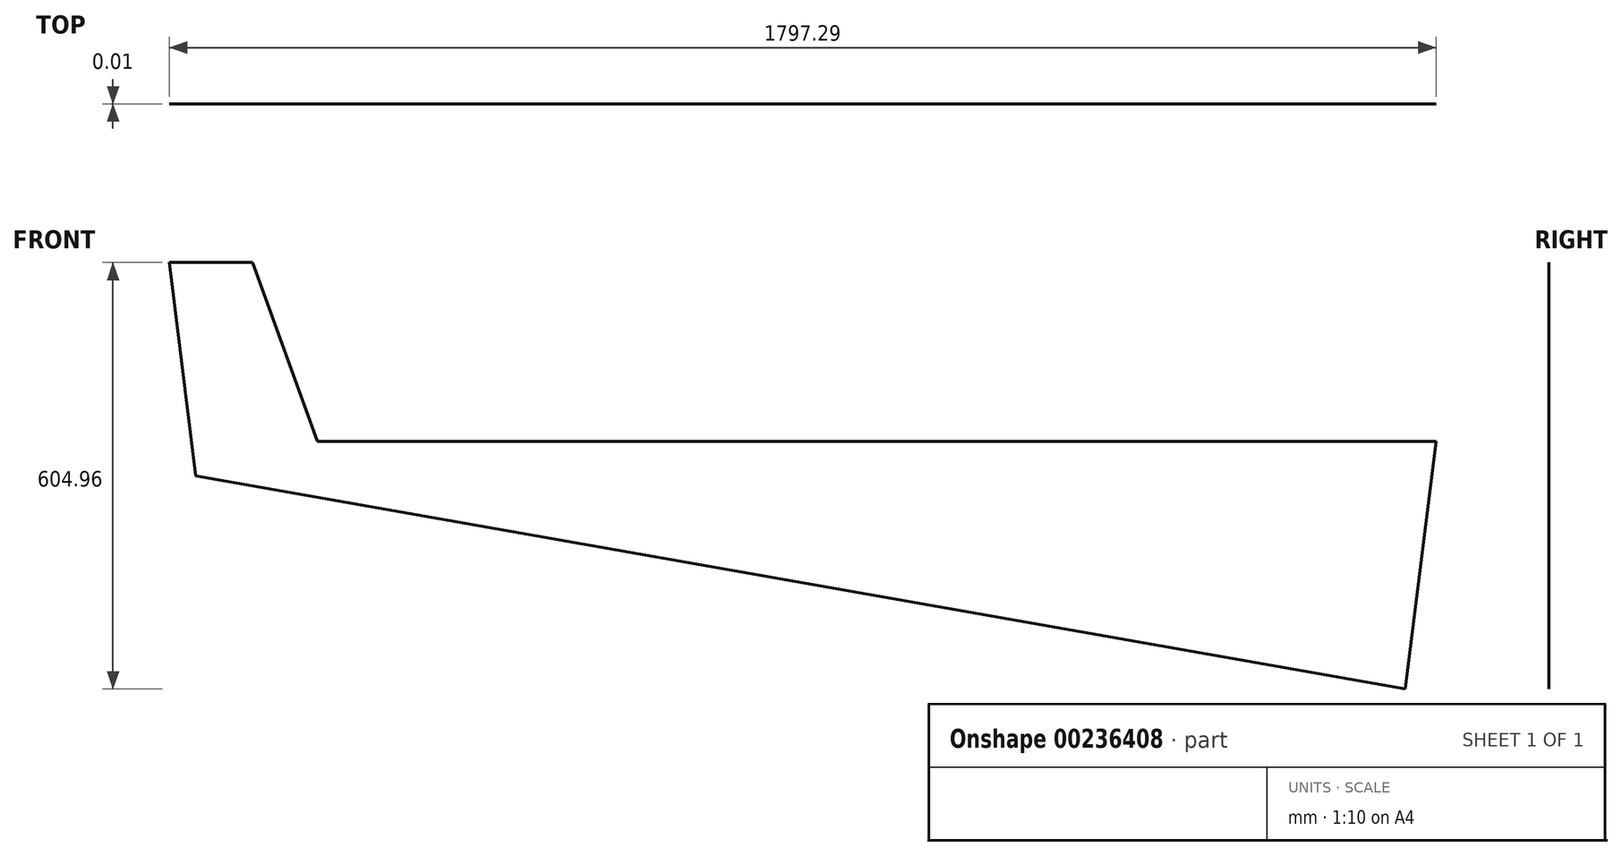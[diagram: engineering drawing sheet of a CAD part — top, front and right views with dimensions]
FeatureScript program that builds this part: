
annotation { "Feature Type Name" : "Feature", "Feature Type Description" : "" }
export const myFeature = defineFeature(function(context is Context, id is Id, definition is map)
    precondition{}
    {
        {
            var Q0;
            Q0=qCreatedBy(makeId("Front.planeOp"),FACE);
            var sketch = newSketch(context, id + "F0", { "sketchPlane" : qUnion([Q0])});
            skLineSegment(sketch, "E0", {"start": v(1065.15, 41.77) * mm, "end": v(1021.62, -309.2) * mm});
            skLineSegment(sketch, "E1", {"start": v(1021.62, -309.2) * mm, "end": v(-694.63, -6.71) * mm});
            skLineSegment(sketch, "E2", {"start": v(-694.63, -6.71) * mm, "end": v(-732.14, 295.77) * mm});
            skLineSegment(sketch, "E3", {"start": v(-732.14, 295.77) * mm, "end": v(-614.32, 295.77) * mm});
            skLineSegment(sketch, "E4", {"start": v(1065.15, 41.77) * mm, "end": v(-521.87, 41.77) * mm});
            skLineSegment(sketch, "E5", {"start": v(-521.87, 41.77) * mm, "end": v(-614.32, 295.77) * mm});
            skSolve(sketch);
        }
        {
            var Q0;
            Q0 = qSketchRegion(id + "F0", true);
            extrude(context, id + "F1", {"entities" : qUnion([Q0]), "depth" : 3 / 406.4 * mm});
        }
    });
